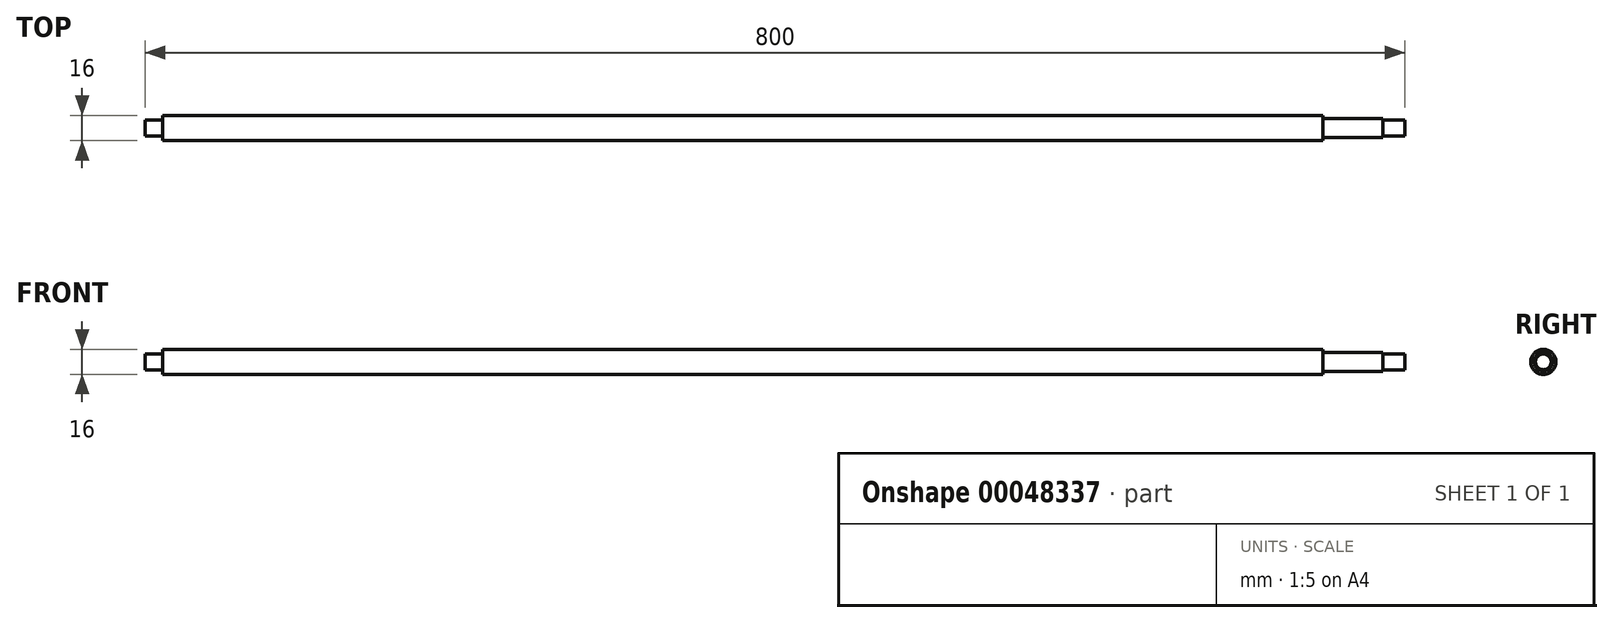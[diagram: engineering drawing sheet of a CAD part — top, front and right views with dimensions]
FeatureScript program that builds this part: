
annotation { "Feature Type Name" : "Feature", "Feature Type Description" : "" }
export const myFeature = defineFeature(function(context is Context, id is Id, definition is map)
    precondition{}
    {
        {
            var Q0;
            Q0=qCreatedBy(makeId("Top.planeOp"),FACE);
            var sketch = newSketch(context, id + "F0", { "sketchPlane" : qUnion([Q0])});
            skLineSegment(sketch, "E0", {"start": v(-350.57, -40.96) * mm, "end": v(449.43, -40.96) * mm});
            skLineSegment(sketch, "E1", {"start": v(-350.57, -40.96) * mm, "end": v(-350.57, -35.96) * mm});
            skLineSegment(sketch, "E2", {"start": v(-350.57, -35.96) * mm, "end": v(-339.57, -35.96) * mm});
            skLineSegment(sketch, "E3", {"start": v(-339.57, -35.96) * mm, "end": v(-339.57, -32.96) * mm});
            skLineSegment(sketch, "E4", {"start": v(-339.57, -32.96) * mm, "end": v(397.43, -32.96) * mm});
            skLineSegment(sketch, "E5", {"start": v(397.43, -32.96) * mm, "end": v(397.43, -34.96) * mm});
            skLineSegment(sketch, "E6", {"start": v(397.43, -34.96) * mm, "end": v(435.43, -34.96) * mm});
            skLineSegment(sketch, "E7", {"start": v(435.43, -34.96) * mm, "end": v(435.43, -35.96) * mm});
            skLineSegment(sketch, "E8", {"start": v(435.43, -35.96) * mm, "end": v(449.43, -35.96) * mm});
            skLineSegment(sketch, "E9", {"start": v(449.43, -35.96) * mm, "end": v(449.43, -40.96) * mm});
            skSolve(sketch);
        }
        {
            var Q0;
            Q0=makeQuery(id+"F0.imprint","IMPRINT",FACE,{"disambiguationData":[TD([[makeQuery(id+"F0.imprint","IMPRINT",EDGE,{"derivedFrom":sQuery(id+"F0.wireOp",EDGE,"E0")}),1.0]])]});
            var Q1;
            Q1=sQuery(id+"F0.wireOp",EDGE,"E0");
            revolve(context, id + "F1", {"entities" : qUnion([Q0]), "axis" : qUnion([Q1]), "revolveType" : RevolveType.FULL});
        }
    });
